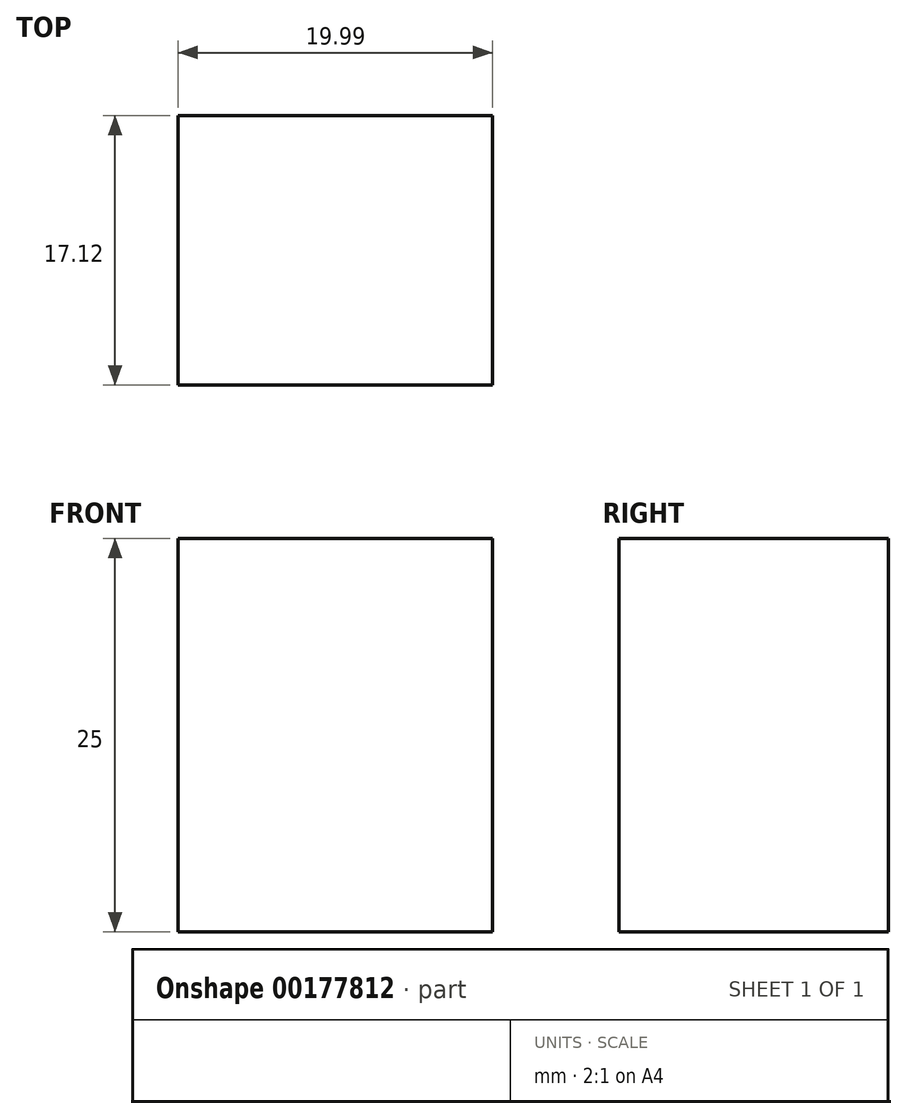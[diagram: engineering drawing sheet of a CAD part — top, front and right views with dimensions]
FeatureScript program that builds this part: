
annotation { "Feature Type Name" : "Feature", "Feature Type Description" : "" }
export const myFeature = defineFeature(function(context is Context, id is Id, definition is map)
    precondition{}
    {
        {
            var Q0;
            Q0=qCreatedBy(makeId("Top.planeOp"),FACE);
            var sketch = newSketch(context, id + "F0", { "sketchPlane" : qUnion([Q0])});
            skLineSegment(sketch, "E0.bottom", {"start": v(-30.85, 15.22) * mm, "end": v(-10.86, 15.22) * mm});
            skLineSegment(sketch, "E0.top", {"start": v(-30.85, -1.9) * mm, "end": v(-10.86, -1.9) * mm});
            skLineSegment(sketch, "E0.left", {"start": v(-30.85, 15.22) * mm, "end": v(-30.85, -1.9) * mm});
            skLineSegment(sketch, "E0.right", {"start": v(-10.86, 15.22) * mm, "end": v(-10.86, -1.9) * mm});
            skSolve(sketch);
        }
        {
            var Q0;
            Q0=makeQuery(id+"F0.imprint","IMPRINT",FACE,{"disambiguationData":[TD([[makeQuery(id+"F0.imprint","IMPRINT",EDGE,{"derivedFrom":sQuery(id+"F0.wireOp",EDGE,"E0.bottom")}),-1.0]])]});
            extrude(context, id + "F1", {"entities" : qUnion([Q0]), "oppositeDirection" : true, "depth" : 25 * mm});
        }
    });
